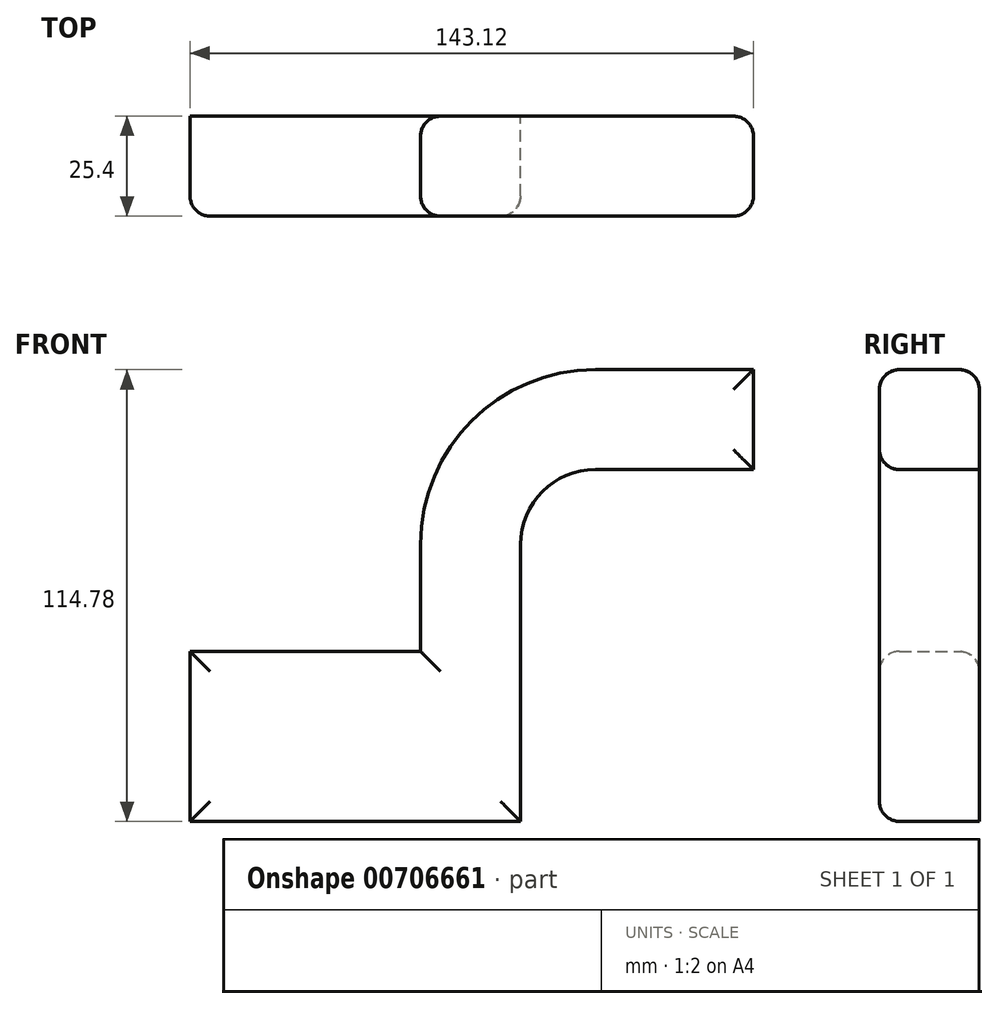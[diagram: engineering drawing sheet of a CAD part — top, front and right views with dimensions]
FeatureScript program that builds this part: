
annotation { "Feature Type Name" : "Feature", "Feature Type Description" : "" }
export const myFeature = defineFeature(function(context is Context, id is Id, definition is map)
    precondition{}
    {
        {
            var Q0;
            Q0=qCreatedBy(makeId("Front.planeOp"),FACE);
            var sketch = newSketch(context, id + "F0", { "sketchPlane" : qUnion([Q0])});
            skLineSegment(sketch, "E0.bottom", {"start": v(-42, -21.46) * mm, "end": v(41.95, -21.46) * mm});
            skLineSegment(sketch, "E0.top", {"start": v(-42, 21.72) * mm, "end": v(41.95, 21.72) * mm});
            skLineSegment(sketch, "E0.left", {"start": v(-42, -21.46) * mm, "end": v(-42, 21.72) * mm});
            skLineSegment(sketch, "E0.right", {"start": v(41.95, -21.46) * mm, "end": v(41.95, 21.72) * mm});
            skLineSegment(sketch, "E1", {"start": v(41.95, 21.72) * mm, "end": v(41.95, 48.9) * mm});
            skArc(sketch, "E2", {"start": v(41.95, 48.9) * mm, "mid": v(47.52, 62.35) * mm, "end": v(60.96, 67.92) * mm});
            skLineSegment(sketch, "E3", {"start": v(60.96, 67.92) * mm, "end": v(101.12, 67.92) * mm});
            skArc(sketch, "E4.0", {"start": v(16.55, 48.9) * mm, "mid": v(29.56, 80.31) * mm, "end": v(60.96, 93.32) * mm});
            skLineSegment(sketch, "E4.1", {"start": v(16.55, 21.72) * mm, "end": v(16.55, 48.9) * mm});
            skLineSegment(sketch, "E5.0", {"start": v(60.96, 93.32) * mm, "end": v(101.12, 93.32) * mm});
            skLineSegment(sketch, "E6", {"start": v(101.12, 93.32) * mm, "end": v(101.12, 67.92) * mm});
            skSolve(sketch);
        }
        {
            var Q0;
            Q0=makeQuery(id+"F0.imprint","IMPRINT",FACE,{"disambiguationData":[TD([[makeQuery(id+"F0.imprint","IMPRINT",EDGE,{"derivedFrom":sQuery(id+"F0.wireOp",EDGE,"E0.bottom")}),1.0]])]});
            var Q1;
            {var subQ0=sQuery(id+"F0.wireOp",EDGE,"E1");Q1=makeQuery(id+"F0.imprint","IMPRINT",FACE,{"disambiguationData":[TD([[makeQuery(id+"F0.imprint","IMPRINT",EDGE,{"derivedFrom":subQ0}),1.0]])]});}
            extrude(context, id + "F1", {"entities" : qUnion([Q0, Q1]), "depth" : 25.4 * mm, "offsetDistance" : 25.4 * mm});
        }
        {
            var Q0;
            Q0=makeQuery(id+"F1.opExtrude","CAP_FACE",FACE,{"disambiguationData":[OSD([sQuery(id+"F0.wireOp",EDGE,"E0.bottom"),sQuery(id+"F0.wireOp",EDGE,"E0.top"),sQuery(id+"F0.wireOp",EDGE,"E0.left"),sQuery(id+"F0.wireOp",EDGE,"E0.right"),sQuery(id+"F0.wireOp",EDGE,"E1"),sQuery(id+"F0.wireOp",EDGE,"E2"),sQuery(id+"F0.wireOp",EDGE,"E3"),sQuery(id+"F0.wireOp",EDGE,"E4.0"),sQuery(id+"F0.wireOp",EDGE,"E4.1"),sQuery(id+"F0.wireOp",EDGE,"E5.0"),sQuery(id+"F0.wireOp",EDGE,"E6")])],"isStart":false});
            var Q1;
            Q1=makeQuery(id+"F1.opExtrude","CAP_EDGE",EDGE,{"disambiguationData":[OSD([sQuery(id+"F0.wireOp",EDGE,"E5.0")])],"isStart":true});
            var Q2;
            Q2=makeQuery(id+"F1.opExtrude","CAP_EDGE",EDGE,{"disambiguationData":[OSD([sQuery(id+"F0.wireOp",EDGE,"E0.top")])],"isStart":true});
            var Q3;
            Q3=makeQuery(id+"F1.opExtrude","CAP_EDGE",EDGE,{"disambiguationData":[OSD([sQuery(id+"F0.wireOp",EDGE,"E6")])],"isStart":true});
            fillet(context, id + "F2", {"entities" : qUnion([Q0, Q1, Q2, Q3]), "radius" : 5.08 * mm, "tangentPropagation" : true, "allowEdgeOverflow" : false});
        }
    });
